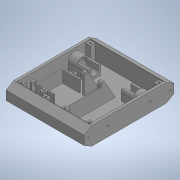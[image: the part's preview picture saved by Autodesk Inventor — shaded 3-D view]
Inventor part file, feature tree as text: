
AUTODESK INVENTOR PART (.ipt)
format: ipt  version: 2020 (Build 240168000, 168)  size: 632,320 bytes
history: native  units: in
note: dims shown in document units (in); Inventor stores cm internally (conversion verified against a paired STEP export)
features: extrude x18, sketch x18, projected_geometry x14, mirror x6, plane x1
ambient origin geometry x8: Origin, YZ Plane, XZ Plane, XY Plane, X Axis, Y Axis, Z Axis, Center Point
bodies: Solid1 (feature_tree)
feature tree (57):
  extrude  "Extrusion1"  Depth=5.9055in
  extrude  "Extrusion2"  TaperAngle=0.0deg  [1 undecoded]
  extrude  "Extrusion3"  Depth=1.063in
  extrude  "Extrusion4"  Depth=0.315in
  extrude  "Extrusion5"  TaperAngle=0.0deg  [1 undecoded]
  extrude  "Extrusion6"  Depth=0.5906in
  mirror  "Mirror1"
  extrude  "Extrusion7"  Depth=0.0787in
  mirror  "Mirror2"
  extrude  "Extrusion8"  Depth=0.6102in
  mirror  "Mirror3"
  plane  "Work Plane1"
  extrude  "Extrusion9"  Depth=0.7874in TaperAngle=0.0deg
  mirror  "Mirror4"
  extrude  "Extrusion10"  Depth=6.063in TaperAngle=0.0deg
  extrude  "Extrusion11"  Depth=0.1575in
  extrude  "Extrusion12"  TaperAngle=0.0deg  [1 undecoded]
  extrude  "Extrusion13"  Depth=0.2756in
  extrude  "Extrusion14"  Depth=0.4331in
  extrude  "Extrusion17"  Depth=2.7559in
  extrude  "Extrusion18"  Depth=0.0413in
  mirror  "Mirror6"
  extrude  "Extrusion19"  TaperAngle=0.0deg  [1 undecoded]
  mirror  "Mirror7"
  extrude  "Extrusion20"  Depth=0.0787in
  sketch  "Sketch1"  dims[d0=1.1811in d1=5.9055in]
  sketch  "Sketch2"  dims[d2=5.1181in d3=0.0in]
  projected_geometry  "Projected Loop1"
  sketch  "Sketch3"  dims[d4=0.1575in d5=1.063in]
  projected_geometry  "Projected Loop2"
  projected_geometry  "Projected Loop3"
  sketch  "Sketch4"  dims[d6=0.0in d8=0.315in]
  sketch  "Sketch5"  dims[d10=0.993in d11=0.0in]
  projected_geometry  "Projected Loop4"
  sketch  "Sketch6"  dims[d12=0.6496in d13=0.5906in]
  sketch  "Sketch7"  dims[d14=1.5748in d15=0.0787in]
  sketch  "Sketch9"  dims[d16=0.5512in d17=0.0in d18=0.6102in]
  sketch  "Sketch10"  dims[d19=0.4803in d20=0.7874in d21=0.0in]
  sketch  "Sketch12"  dims[d22=0.1654in d23=6.063in d24=0.0in]
  projected_geometry  "Projected Loop6"
  projected_geometry  "Projected Loop7"
  projected_geometry  "Projected Loop8"
  sketch  "Sketch13"  dims[d25=0.5114in d26=0.1575in]
  sketch  "Sketch14"  dims[d27=1.5748in d28=0.0in d29=0.0in]
  sketch  "Sketch15"  dims[d30=0.1575in d31=0.2756in]
  projected_geometry  "Projected Loop15"
  sketch  "Sketch16"  dims[d32=0.0in d33=0.4331in]
  projected_geometry  "Projected Loop19"
  projected_geometry  "Projected Loop20"
  projected_geometry  "Projected Loop21"
  projected_geometry  "Projected Loop22"
  projected_geometry  "Projected Loop23"
  projected_geometry  "Projected Loop24"
  sketch  "Sketch20"  dims[d34=0.0827in d38=2.7559in]
  sketch  "Sketch21"  dims[d40=0.0413in d41=0.0909in]
  sketch  "Sketch22"  dims[d42=0.2362in d43=0.0in]
  sketch  "Sketch23"  dims[d44=60.0deg d45=0.0787in d46=0.315in d48=0.993in d49=0.0in d53=0.2756in d54=0.0in d55=0.4724in d56=1.2008in d57=1.6142in d58=1.5945in d59=0.0787in d60=0.0787in d62=0.315in d63=0.7677in d64=0.0in d66=0.1476in d67=0.2756in d68=0.0in d69=0.7874in d70=0.2953in d71=0.1181in d72=0.0in d89=0.0157in d90=0.0157in d91=0.1476in d92=0.1476in d96=0.315in d97=0.1575in d98=0.1181in d99=0.0in d102=0.1772in d104=0.3346in d105=135.0deg d106=0.2362in d107=0.0in d108=0.0394in d109=0.0in d110=0.063in d111=0.0394in d112=0.0in]
note: 4 required parameter values undecoded (feature->parameter linkage not recoverable at this tier; creation-order binding heuristic only, values carry confidence <= 0.55)
